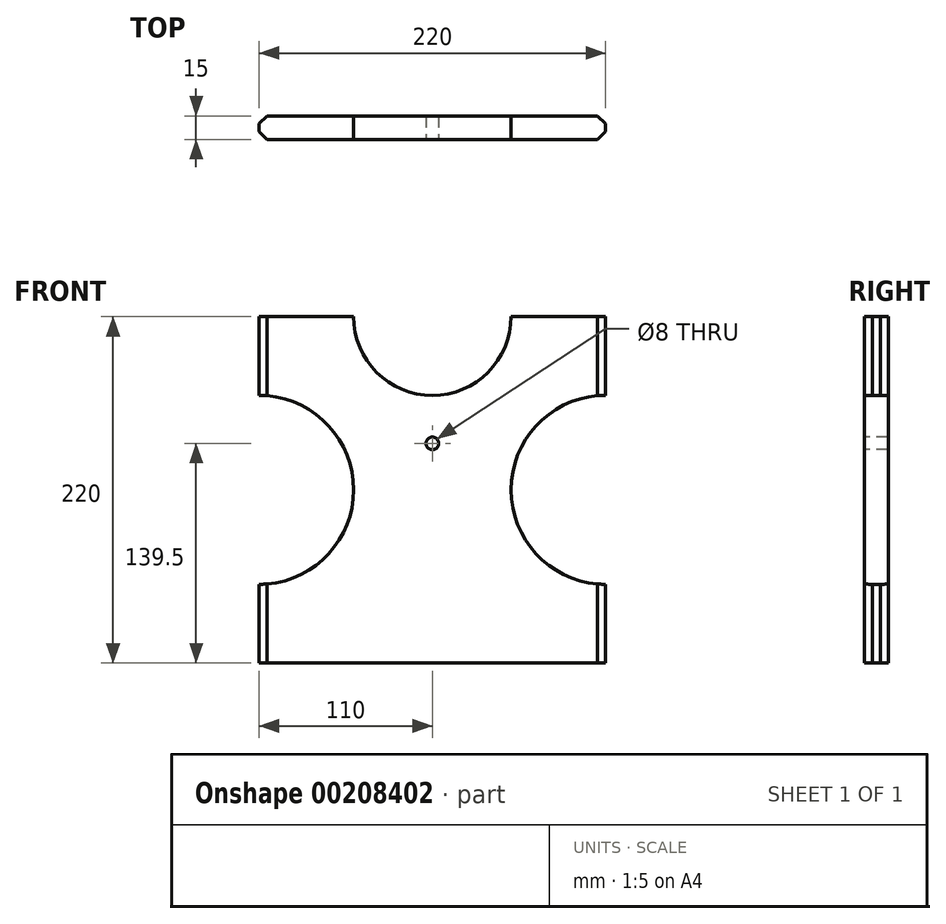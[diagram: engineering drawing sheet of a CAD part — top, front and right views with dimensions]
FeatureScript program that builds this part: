
annotation { "Feature Type Name" : "Feature", "Feature Type Description" : "" }
export const myFeature = defineFeature(function(context is Context, id is Id, definition is map)
    precondition{}
    {
        {
            var Q0;
            Q0=qCreatedBy(makeId("Front.planeOp"),FACE);
            var sketch = newSketch(context, id + "F0", { "sketchPlane" : qUnion([Q0])});
            skLineSegment(sketch, "E0.bottom", {"start": v(110, 110) * mm, "end": v(-110, 110) * mm});
            skLineSegment(sketch, "E0.top", {"start": v(110, -110) * mm, "end": v(-110, -110) * mm});
            skLineSegment(sketch, "E0.left", {"start": v(110, 110) * mm, "end": v(110, -110) * mm});
            skLineSegment(sketch, "E0.right", {"start": v(-110, 110) * mm, "end": v(-110, -110) * mm});
            skPoint(sketch, "E0.middle", {"position": v(0, 0) * mm});
            skLineSegment(sketch, "E1", {"start": v(0, 110) * mm, "end": v(0, 197.37) * mm});
            skLineSegment(sketch, "E2", {"start": v(0, 197.37) * mm, "end": v(0, 197.37) * mm});
            skLineSegment(sketch, "E3", {"start": v(0, 197.37) * mm, "end": v(-110, 110) * mm});
            skLineSegment(sketch, "E4", {"start": v(110, 110) * mm, "end": v(0, 197.37) * mm});
            skCircle(sketch, "E5", {"center": v(-110, 0) * mm, "radius": 60 * mm});
            skCircle(sketch, "E6", {"center": v(110, 0) * mm, "radius": 60 * mm});
            skCircle(sketch, "E7", {"center": v(0, 110) * mm, "radius": 50 * mm});
            skSolve(sketch);
        }
        {
            var Q0;
            Q0=makeQuery(id+"F0.imprint","IMPRINT",FACE,{"disambiguationData":[TD([[makeQuery(id+"F0.imprint","IMPRINT",EDGE,{"derivedFrom":sQuery(id+"F0.wireOp",EDGE,"E0.top")}),-1.0]])]});
            extrude(context, id + "F1", {"entities" : qUnion([Q0]), "depth" : 15 * mm, "symmetric" : true});
        }
        {
            var Q0;
            Q0=makeQuery(id+"F1.opExtrude","CAP_EDGE",EDGE,{"disambiguationData":[OSD([sQuery(id+"F0.wireOp",EDGE,"E3")])],"isStart":true});
            var Q1;
            Q1=makeQuery(id+"F1.opExtrude","CAP_EDGE",EDGE,{"disambiguationData":[OSD([sQuery(id+"F0.wireOp",EDGE,"E4")])],"isStart":true});
            var Q2;
            Q2=makeQuery(id+"F1.opExtrude","CAP_EDGE",EDGE,{"disambiguationData":[OSD([sQuery(id+"F0.wireOp",EDGE,"E0.right")])],"isStart":true});
            var Q3;
            Q3=makeQuery(id+"F1.opExtrude","CAP_EDGE",EDGE,{"disambiguationData":[OSD([sQuery(id+"F0.wireOp",EDGE,"E0.left")])],"isStart":true});
            chamfer(context, id + "F2", {"entities" : qUnion([Q0, Q1, Q2, Q3]), "width" : 5 * mm, "tangentPropagation" : true});
        }
        {
            var Q0;
            Q0=makeQuery(id+"F1.opExtrude","CAP_EDGE",EDGE,{"disambiguationData":[OSD([sQuery(id+"F0.wireOp",EDGE,"E0.right")])],"isStart":false});
            chamfer(context, id + "F3", {"entities" : qUnion([Q0]), "width" : 5 * mm, "tangentPropagation" : true});
        }
        {
            var Q0;
            Q0=makeQuery(id+"F1.opExtrude","CAP_EDGE",EDGE,{"disambiguationData":[OSD([sQuery(id+"F0.wireOp",EDGE,"E0.left")])],"isStart":false});
            chamfer(context, id + "F4", {"entities" : qUnion([Q0]), "width" : 5 * mm, "tangentPropagation" : true});
        }
        {
            var Q0;
            Q0=makeQuery(id+"F1.opExtrude","CAP_FACE",FACE,{"disambiguationData":[OSD([sQuery(id+"F0.wireOp",EDGE,"E0.top"),sQuery(id+"F0.wireOp",EDGE,"E0.left"),sQuery(id+"F0.wireOp",EDGE,"E0.right"),sQuery(id+"F0.wireOp",EDGE,"E3"),sQuery(id+"F0.wireOp",EDGE,"E4")])],"isStart":false});
            var sketch = newSketch(context, id + "F5", { "sketchPlane" : qUnion([Q0])});
            skCircle(sketch, "E8", {"center": v(0, 29.5) * mm, "radius": 4 * mm});
            skSolve(sketch);
        }
        {
            var Q0;
            Q0 = qSketchRegion(id + "F5", true);
            extrude(context, id + "F6", {"entities" : qUnion([Q0]), "operationType" : NewBodyOperationType.REMOVE, "endBound" : BoundingType.THROUGH_ALL, "oppositeDirection" : true, "depth" : 25 * mm});
        }
    });
